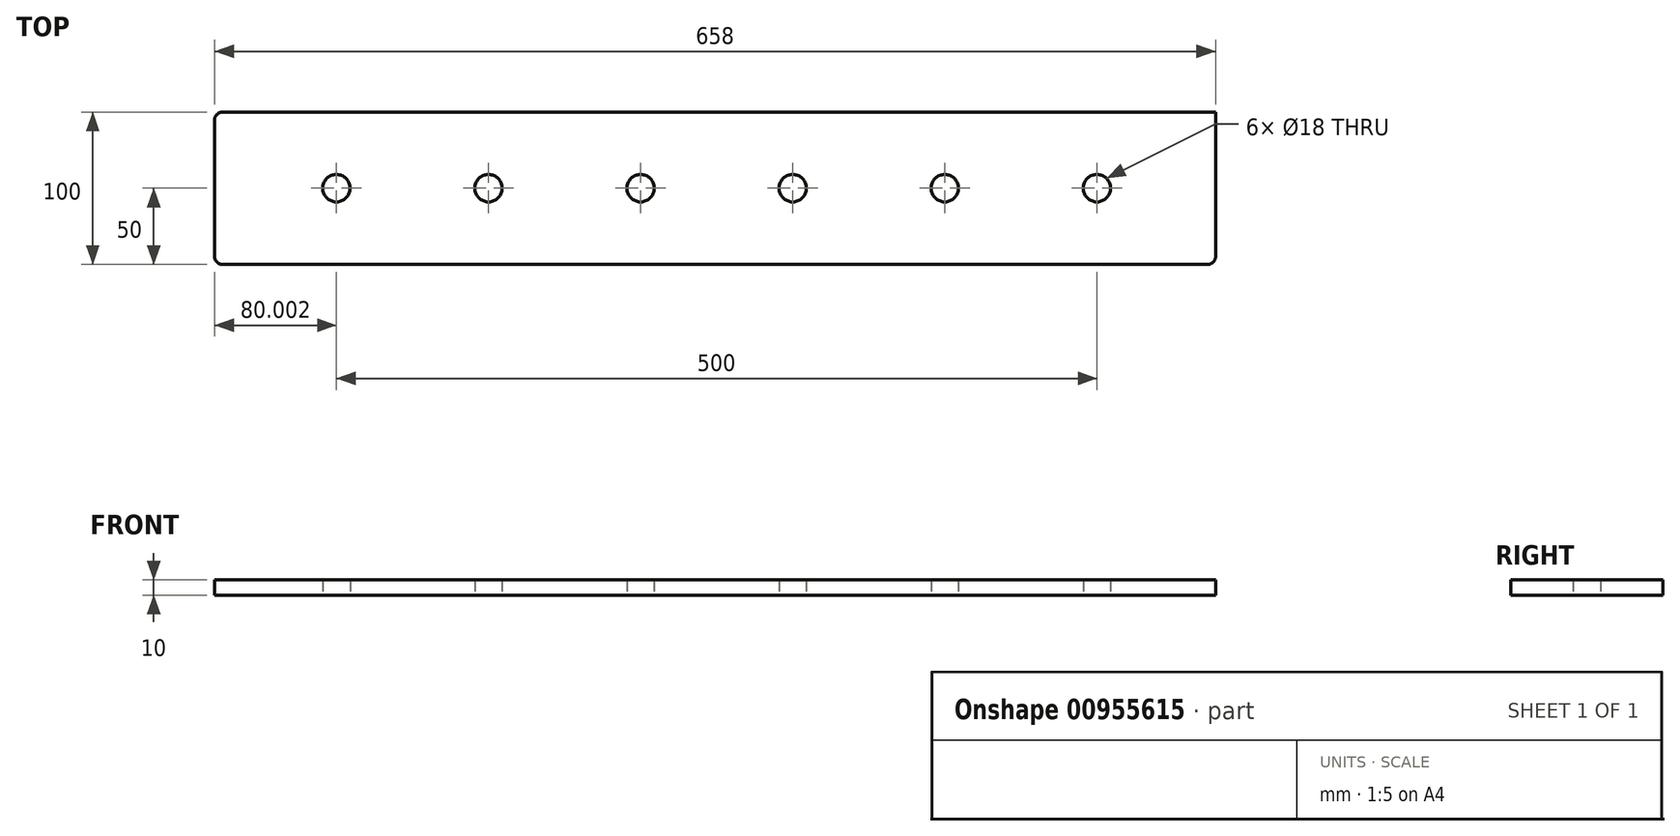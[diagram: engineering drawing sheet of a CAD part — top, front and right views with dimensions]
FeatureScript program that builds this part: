
annotation { "Feature Type Name" : "Feature", "Feature Type Description" : "" }
export const myFeature = defineFeature(function(context is Context, id is Id, definition is map)
    precondition{}
    {
        {
            var Q0;
            Q0=qCreatedBy(makeId("Top.planeOp"),FACE);
            var sketch = newSketch(context, id + "F0", { "sketchPlane" : qUnion([Q0])});
            skLineSegment(sketch, "E0", {"start": v(-330.62, -100) * mm, "end": v(-330.62, -50) * mm});
            skLineSegment(sketch, "E1", {"start": v(-330.62, -50) * mm, "end": v(-250.62, -50) * mm});
            skCircle(sketch, "E2", {"center": v(-250.62, -50) * mm, "radius": 9 * mm});
            skCircle(sketch, "E3.1.0.0", {"center": v(-150.62, -50) * mm, "radius": 9 * mm});
            skCircle(sketch, "E3.2.0.0", {"center": v(-50.62, -50) * mm, "radius": 9 * mm});
            skCircle(sketch, "E3.3.0.0", {"center": v(49.38, -50) * mm, "radius": 9 * mm});
            skCircle(sketch, "E3.4.0.0", {"center": v(149.38, -50) * mm, "radius": 9 * mm});
            skCircle(sketch, "E3.5.0.0", {"center": v(249.38, -50) * mm, "radius": 9 * mm});
            skLineSegment(sketch, "E3.direction1", {"start": v(-250.62, -50) * mm, "end": v(-150.62, -50) * mm, "construction": true});
            skLineSegment(sketch, "E4.bottom", {"start": v(-330.62, 0) * mm, "end": v(327.38, 0) * mm});
            skLineSegment(sketch, "E4.top", {"start": v(-330.62, -100) * mm, "end": v(327.38, -100) * mm});
            skLineSegment(sketch, "E4.left", {"start": v(-330.62, 0) * mm, "end": v(-330.62, -100) * mm});
            skLineSegment(sketch, "E4.right", {"start": v(327.38, 0) * mm, "end": v(327.38, -100) * mm});
            skSolve(sketch);
        }
        {
            var Q0;
            Q0 = qSketchRegion(id + "F0", true);
            extrude(context, id + "F1", {"entities" : qUnion([Q0]), "depth" : 10 * mm, "offsetDistance" : 25 * mm});
        }
        {
            var Q0;
            Q0=makeQuery(id+"F1.opExtrude","SWEPT_EDGE",EDGE,{"disambiguationData":[OSD([sQuery(id+"F0.wireOp",EDGE,"E4.top"),sQuery(id+"F0.wireOp",EDGE,"E4.left")])]});
            var Q1;
            Q1=makeQuery(id+"F1.opExtrude","SWEPT_EDGE",EDGE,{"disambiguationData":[OSD([sQuery(id+"F0.wireOp",EDGE,"E4.top"),sQuery(id+"F0.wireOp",EDGE,"E4.right")])]});
            fillet(context, id + "F2", {"entities" : qUnion([Q0, Q1]), "radius" : 5 * mm, "tangentPropagation" : true, "allowEdgeOverflow" : false});
        }
    });
